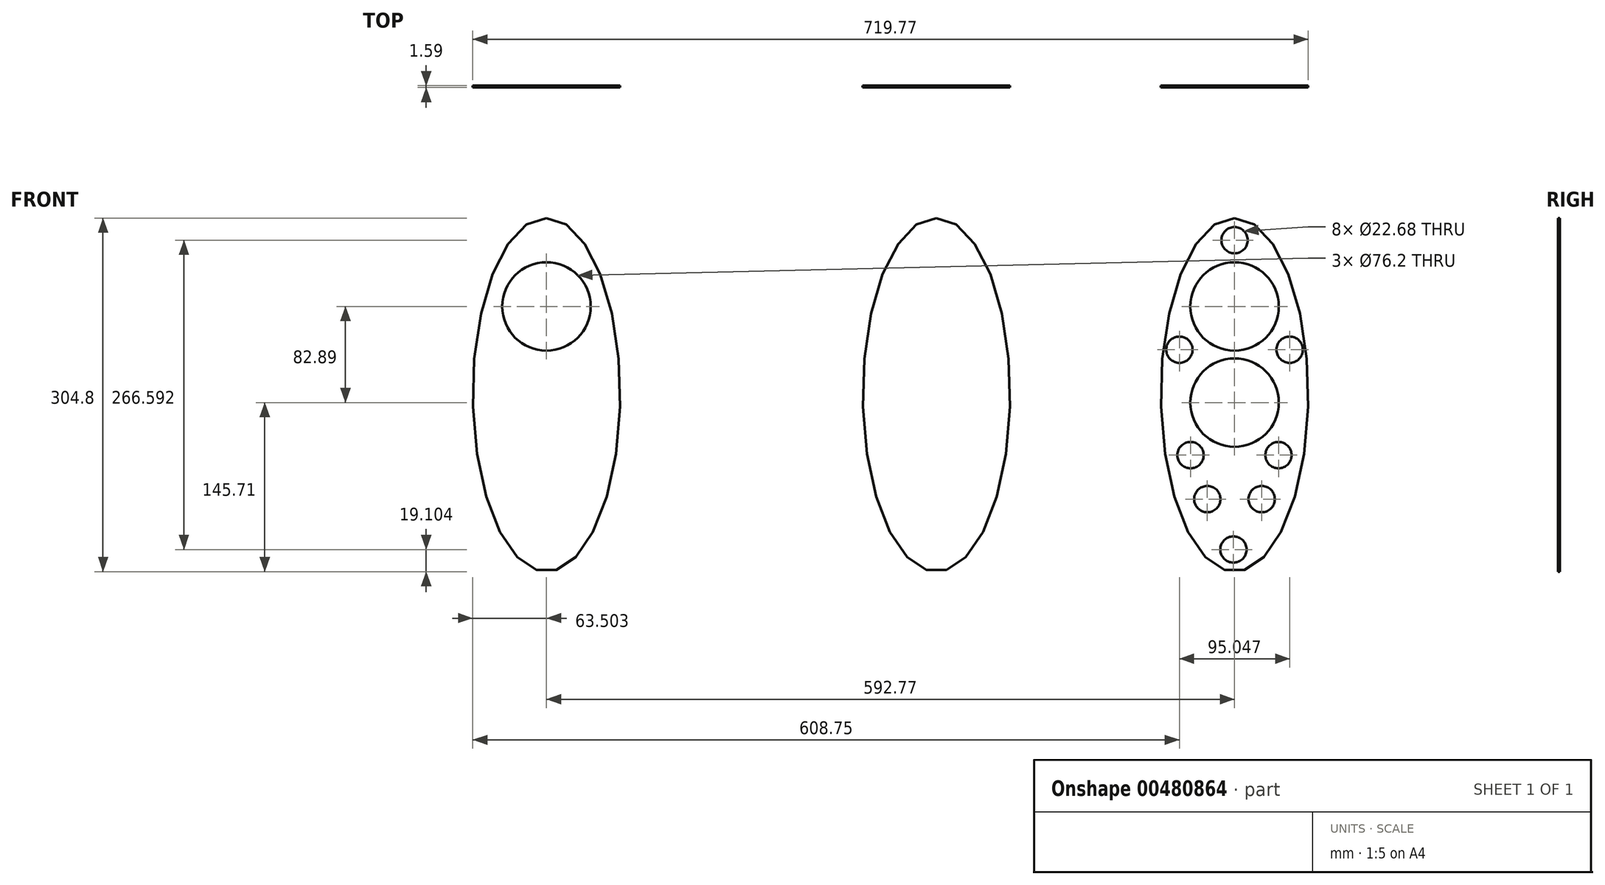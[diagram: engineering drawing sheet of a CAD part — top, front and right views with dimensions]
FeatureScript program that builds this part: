
annotation { "Feature Type Name" : "Feature", "Feature Type Description" : "" }
export const myFeature = defineFeature(function(context is Context, id is Id, definition is map)
    precondition{}
    {
        {
            var Q0;
            Q0=qCreatedBy(makeId("Front.planeOp"),FACE);
            var sketch = newSketch(context, id + "F0", { "sketchPlane" : qUnion([Q0])});
            skEllipse(sketch, "E0", {"center": v(283.02, 0) * mm, "majorRadius": 152.4 * mm, "minorRadius": 63.5 * mm, "majorAxis": v(0, 1)});
            skLineSegment(sketch, "E1", {"start": v(283.02, 0) * mm, "end": v(283.02, 152.4) * mm, "construction": true});
            skLineSegment(sketch, "E2", {"start": v(283.02, 0) * mm, "end": v(283.02, -152.4) * mm, "construction": true});
            skCircle(sketch, "E3", {"center": v(283.02, 76.2) * mm, "radius": 38.1 * mm});
            skCircle(sketch, "E4", {"center": v(235.5, 38.93) * mm, "radius": 11.34 * mm});
            skCircle(sketch, "E5", {"center": v(259.6, -89.88) * mm, "radius": 11.34 * mm});
            skCircle(sketch, "E6", {"center": v(245.14, -52) * mm, "radius": 11.34 * mm});
            skCircle(sketch, "E7.MirrorC", {"center": v(330.55, 38.93) * mm, "radius": 11.34 * mm});
            skCircle(sketch, "E8.MirrorC", {"center": v(306.44, -89.88) * mm, "radius": 11.34 * mm});
            skCircle(sketch, "E9.MirrorC", {"center": v(320.9, -52) * mm, "radius": 11.34 * mm});
            skCircle(sketch, "E10", {"center": v(283.02, 133.3) * mm, "radius": 11.34 * mm});
            skCircle(sketch, "E11.MirrorC", {"center": v(282.1, -133.3) * mm, "radius": 11.34 * mm});
            skCircle(sketch, "E12", {"center": v(283.02, -6.69) * mm, "radius": 38.1 * mm});
            skSolve(sketch);
        }
        {
            var Q0;
            Q0=qCreatedBy(makeId("Front.planeOp"),FACE);
            var sketch = newSketch(context, id + "F1", { "sketchPlane" : qUnion([Q0])});
            skEllipse(sketch, "E13", {"center": v(26.23, 0) * mm, "majorRadius": 152.4 * mm, "minorRadius": 63.5 * mm, "majorAxis": v(0, 1)});
            skLineSegment(sketch, "E14", {"start": v(-141.76, 154.37) * mm, "end": v(-141.76, -132.28) * mm, "construction": true});
            skEllipse(sketch, "E15.MirrorC", {"center": v(-309.75, 0) * mm, "majorRadius": 152.4 * mm, "minorRadius": 63.5 * mm, "majorAxis": v(0, 1)});
            skCircle(sketch, "E16", {"center": v(-309.75, 76.2) * mm, "radius": 38.1 * mm});
            skLineSegment(sketch, "E17", {"start": v(-309.75, 76.2) * mm, "end": v(-309.75, 152.4) * mm, "construction": true});
            skSolve(sketch);
        }
        {
            var Q0;
            Q0 = qSketchRegion(id + "F1", true);
            extrude(context, id + "F2", {"entities" : qUnion([Q0]), "depth" : 1.59 * mm});
        }
        {
            var Q0;
            Q0=makeQuery(id+"F0.imprint","IMPRINT",FACE,{"disambiguationData":[TD([[makeQuery(id+"F0.imprint","IMPRINT",EDGE,{"derivedFrom":sQuery(id+"F0.wireOp",EDGE,"E0")}),1.0]])]});
            extrude(context, id + "F3", {"entities" : qUnion([Q0]), "depth" : 1.59 * mm});
        }
    });
